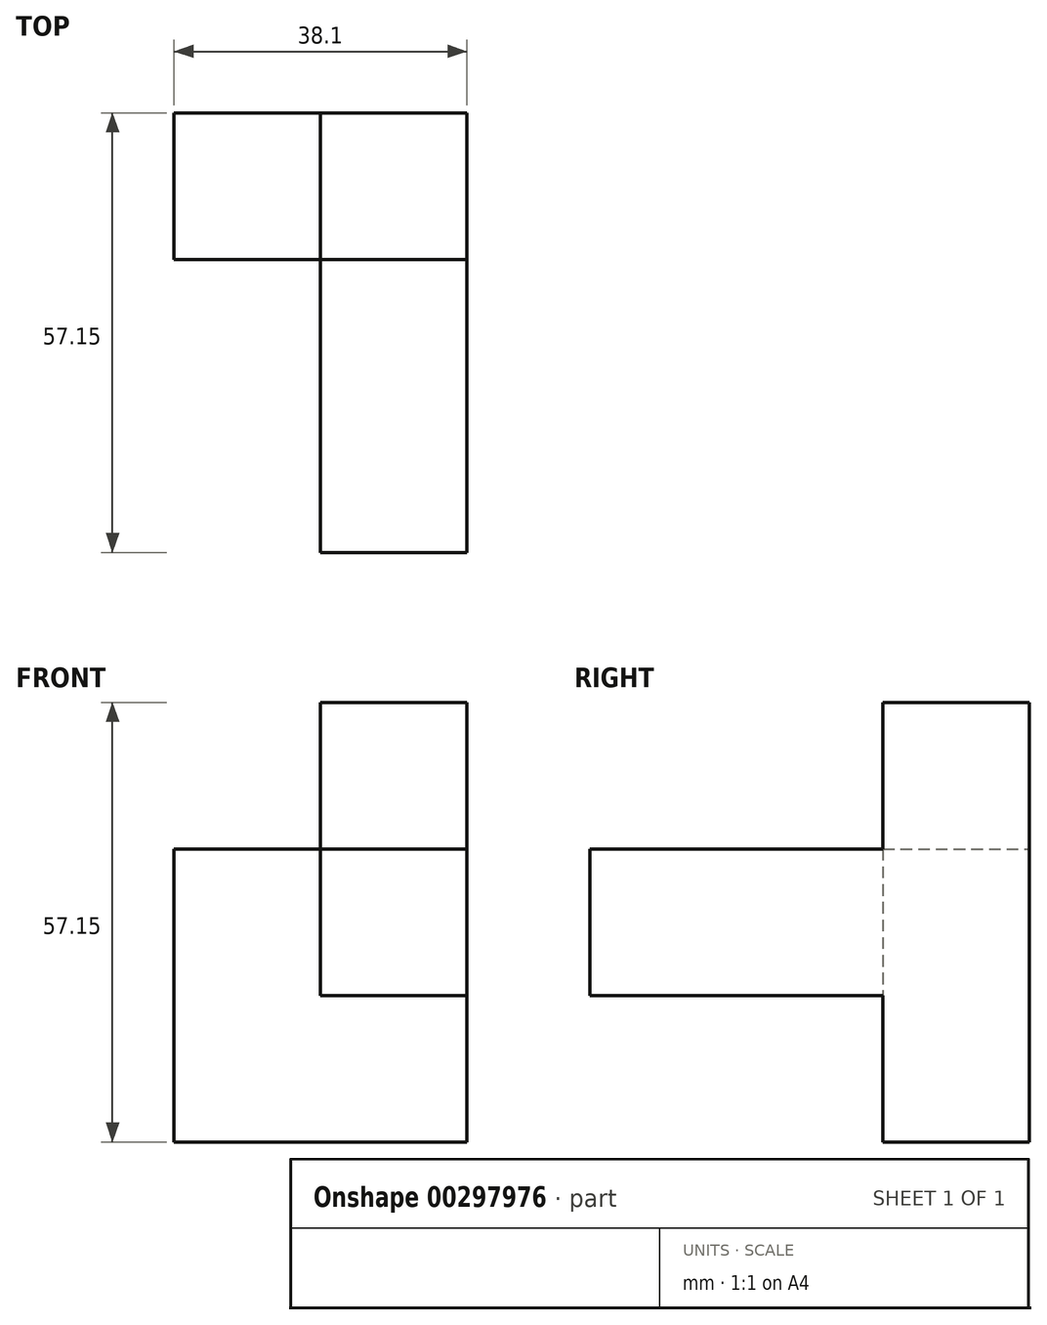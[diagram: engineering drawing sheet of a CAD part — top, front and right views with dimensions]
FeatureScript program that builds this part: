
annotation { "Feature Type Name" : "Feature", "Feature Type Description" : "" }
export const myFeature = defineFeature(function(context is Context, id is Id, definition is map)
    precondition{}
    {
        {
            var Q0;
            Q0=qCreatedBy(makeId("Front.planeOp"),FACE);
            var sketch = newSketch(context, id + "F0", { "sketchPlane" : qUnion([Q0])});
            skLineSegment(sketch, "E0.bottom", {"start": v(0, 0) * mm, "end": v(38.1, 0) * mm});
            skLineSegment(sketch, "E0.top", {"start": v(0, 38.1) * mm, "end": v(19.05, 38.1) * mm});
            skLineSegment(sketch, "E0.left", {"start": v(0, 0) * mm, "end": v(0, 38.1) * mm});
            skLineSegment(sketch, "E0.right", {"start": v(38.1, 0) * mm, "end": v(38.1, 38.1) * mm});
            skLineSegment(sketch, "E1.top", {"start": v(19.05, 57.15) * mm, "end": v(38.1, 57.15) * mm});
            skLineSegment(sketch, "E1.left", {"start": v(19.05, 38.1) * mm, "end": v(19.05, 57.15) * mm});
            skLineSegment(sketch, "E1.right", {"start": v(38.1, 38.1) * mm, "end": v(38.1, 57.15) * mm});
            skSolve(sketch);
        }
        {
            var Q0;
            Q0 = qSketchRegion(id + "F0", true);
            extrude(context, id + "F1", {"entities" : qUnion([Q0]), "depth" : 19.05 * mm});
        }
        {
            var Q0;
            Q0=makeQuery(id+"F1.opExtrude","CAP_FACE",FACE,{"disambiguationData":[OSD([sQuery(id+"F0.wireOp",EDGE,"E0.bottom"),sQuery(id+"F0.wireOp",EDGE,"E0.top"),sQuery(id+"F0.wireOp",EDGE,"E0.left"),sQuery(id+"F0.wireOp",EDGE,"E0.right"),sQuery(id+"F0.wireOp",EDGE,"E1.top"),sQuery(id+"F0.wireOp",EDGE,"E1.left"),sQuery(id+"F0.wireOp",EDGE,"E1.right")])],"isStart":false});
            var sketch = newSketch(context, id + "F2", { "sketchPlane" : qUnion([Q0])});
            skLineSegment(sketch, "E2.bottom", {"start": v(19.05, 38.1) * mm, "end": v(38.1, 38.1) * mm});
            skLineSegment(sketch, "E2.top", {"start": v(19.05, 19.05) * mm, "end": v(38.1, 19.05) * mm});
            skLineSegment(sketch, "E2.left", {"start": v(19.05, 38.1) * mm, "end": v(19.05, 19.05) * mm});
            skLineSegment(sketch, "E2.right", {"start": v(38.1, 38.1) * mm, "end": v(38.1, 19.05) * mm});
            skSolve(sketch);
        }
        {
            var Q0;
            Q0 = qSketchRegion(id + "F2", true);
            extrude(context, id + "F3", {"entities" : qUnion([Q0]), "operationType" : NewBodyOperationType.ADD, "depth" : 38.1 * mm});
        }
    });
